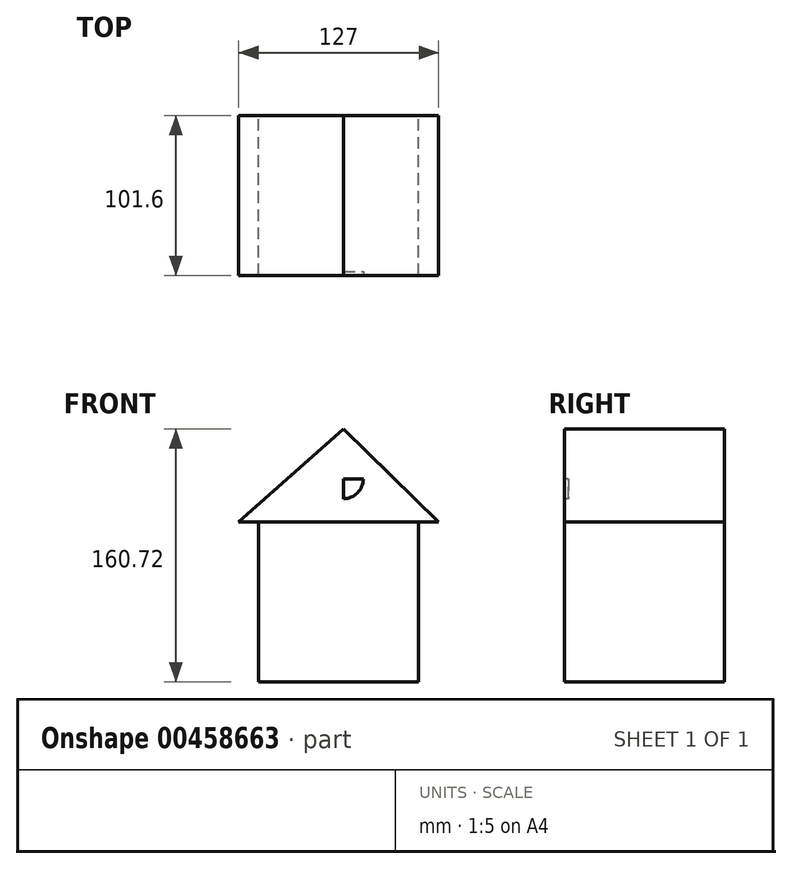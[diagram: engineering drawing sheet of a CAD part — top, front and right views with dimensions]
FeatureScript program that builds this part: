
annotation { "Feature Type Name" : "Feature", "Feature Type Description" : "" }
export const myFeature = defineFeature(function(context is Context, id is Id, definition is map)
    precondition{}
    {
        {
            var Q0;
            Q0=qCreatedBy(makeId("Top.planeOp"),FACE);
            var sketch = newSketch(context, id + "F0", { "sketchPlane" : qUnion([Q0])});
            skLineSegment(sketch, "E0.bottom", {"start": v(47.9, -50.8) * mm, "end": v(-53.7, -50.8) * mm});
            skLineSegment(sketch, "E0.top", {"start": v(47.9, 50.8) * mm, "end": v(-53.7, 50.8) * mm});
            skLineSegment(sketch, "E0.left", {"start": v(47.9, -50.8) * mm, "end": v(47.9, 50.8) * mm});
            skLineSegment(sketch, "E0.right", {"start": v(-53.7, -50.8) * mm, "end": v(-53.7, 50.8) * mm});
            skPoint(sketch, "E0.middle", {"position": v(-2.9, 0) * mm});
            skSolve(sketch);
        }
        {
            var Q0;
            Q0 = qSketchRegion(id + "F0", true);
            extrude(context, id + "F1", {"entities" : qUnion([Q0]), "depth" : 101.6 * mm});
        }
        {
            var Q0;
            Q0=makeQuery(id+"F1.opExtrude","SWEPT_FACE",FACE,{"disambiguationData":[OSD([sQuery(id+"F0.wireOp",EDGE,"E0.bottom")])]});
            var sketch = newSketch(context, id + "F2", { "sketchPlane" : qUnion([Q0])});
            skLineSegment(sketch, "E1", {"start": v(-66.4, 127) * mm, "end": v(0, 186.12) * mm});
            skLineSegment(sketch, "E2", {"start": v(0, 186.12) * mm, "end": v(60.6, 127) * mm});
            skLineSegment(sketch, "E3", {"start": v(60.6, 127) * mm, "end": v(-66.4, 127) * mm});
            skSolve(sketch);
        }
        {
            var Q0;
            Q0=makeQuery(id+"F2.imprint","IMPRINT",FACE,{"disambiguationData":[TD([[makeQuery(id+"F2.imprint","IMPRINT",EDGE,{"derivedFrom":sQuery(id+"F2.wireOp",EDGE,"E1")}),-1.0]])]});
            extrude(context, id + "F3", {"entities" : qUnion([Q0]), "operationType" : NewBodyOperationType.ADD, "oppositeDirection" : true, "depth" : 101.6 * mm});
        }
        {
            var Q0;
            Q0=makeQuery(id+"F3.opExtrude","SWEPT_BODY",BODY,{"disambiguationData":[OSD([sQuery(id+"F2.wireOp",EDGE,"E1"),sQuery(id+"F2.wireOp",EDGE,"E2"),sQuery(id+"F2.wireOp",EDGE,"E3")])]});
            var Q1;
            Q1=qCreatedBy(makeId("Origin.pointOp"),VERTEX);
            transform(context, id + "F4", {"entities" : qUnion([Q0]), "transformType" : TransformType.TRANSLATION_3D, "dx" : 0 * mm, "dy" : 0 * mm, "dz" : -25.4 * mm, "makeCopy" : false});
        }
        {
            var Q0;
            Q0=makeQuery(id+"F3.opExtrude","CAP_FACE",FACE,{"disambiguationData":[OSD([sQuery(id+"F2.wireOp",EDGE,"E1"),sQuery(id+"F2.wireOp",EDGE,"E2"),sQuery(id+"F2.wireOp",EDGE,"E3")])],"isStart":true});
            var sketch = newSketch(context, id + "F5", { "sketchPlane" : qUnion([Q0])});
            skCircle(sketch, "E4", {"center": v(0, 129.11) * mm, "radius": 12.7 * mm});
            skLineSegment(sketch, "E5", {"start": v(0, 141.81) * mm, "end": v(0, 116.41) * mm});
            skLineSegment(sketch, "E6", {"start": v(-12.7, 129.11) * mm, "end": v(12.7, 129.11) * mm});
            skSolve(sketch);
        }
        {
            var Q0;
            Q0=makeQuery(id+"F5.imprint","IMPRINT",FACE,{"disambiguationData":[TD([[makeQuery(id+"F5.imprint","IMPRINT",EDGE,{"derivedFrom":sQuery(id+"F5.wireOp",EDGE,"E4")}),1.0]])]});
            var sketch = newSketch(context, id + "F6", { "sketchPlane" : qUnion([Q0])});
            skSolve(sketch);
        }
        {
            var Q0;
            Q0=makeQuery(id+"F6.imprint","IMPRINT",FACE,{"disambiguationData":[TD([[makeQuery(id+"F6.imprint","IMPRINT",EDGE,{"derivedFrom":makeQuery(id+"F5.imprint","IMPRINT",EDGE,{"derivedFrom":sQuery(id+"F5.wireOp",EDGE,"E4")})}),1.0]])]});
            extrude(context, id + "F7", {"entities" : qUnion([Q0]), "operationType" : NewBodyOperationType.REMOVE, "oppositeDirection" : true, "depth" : 2.54 * mm});
        }
    });
